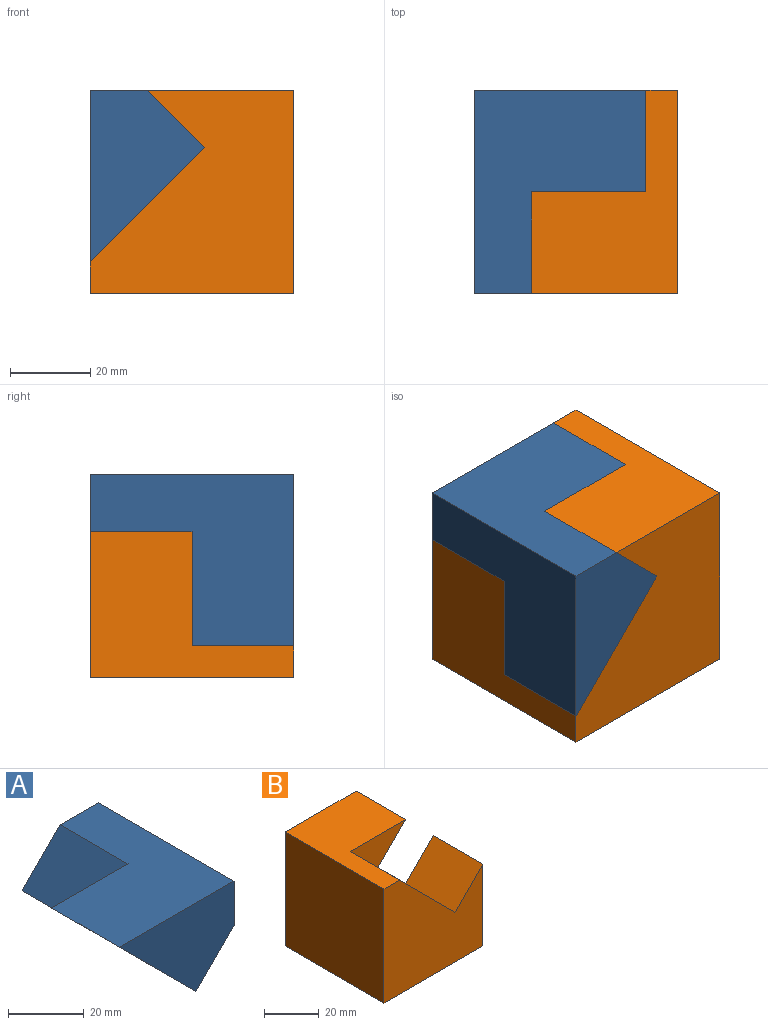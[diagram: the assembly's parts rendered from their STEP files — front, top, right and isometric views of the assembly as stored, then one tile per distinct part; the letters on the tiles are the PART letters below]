
ASSEMBLY  parts=2 mates=1
PART A: 9 faces, bbox 42.9x50.8x42.9 mm
  f0: plane 25.4x14.29mm, normal (-0.71,0,0.71), area 513.2mm2, adj f1,f3,f4,f8
  f1: plane 50.8x42.86mm, normal (-0.71,0,-0.71), area 2052.9mm2, adj f0,f2,f3,f4,f5,f6,f7,f8
  f2: plane 50.8x42.86mm, normal (1,0,0), area 1451.6mm2, adj f1,f3,f4,f5,f6,f7
  f3: plane 50.8x42.86mm, normal (0,0,1), area 1451.6mm2, adj f0,f1,f2,f4,f7,f8
  f4: plane 42.86x28.58mm, normal (0,1,0), area 714.5mm2, adj f0,f1,f2,f3
  f5: plane 28.58x14.29mm, normal (0,-1,0), area 204.1mm2, adj f1,f2,f6
  f6: plane 25.4x14.29mm, normal (0.71,0,-0.71), area 513.2mm2, adj f1,f2,f5,f7
  f7: plane 42.86x28.58mm, normal (0,-1,0), area 714.5mm2, adj f1,f2,f3,f6
  f8: plane 28.58x14.29mm, normal (0,1,0), area 204.1mm2, adj f0,f1,f3
PART B: 11 faces, bbox 50.8x50.8x50.8 mm
  f0: plane 28.58x14.29mm, normal (0,-1,0), area 204.1mm2, adj f1,f2,f3
  f1: plane 50.8x42.86mm, normal (0.71,0,0.71), area 2052.9mm2, adj f0,f2,f3,f6,f7,f8,f9,f10
  f2: plane 25.4x14.29mm, normal (0.71,0,-0.71), area 513.2mm2, adj f0,f1,f3,f7
  f3: plane 50.8x36.51mm, normal (0,0,1), area 1129mm2, adj f0,f1,f2,f4,f7,f9
  f4: plane 50.8x50.8mm, normal (-1,0,0), area 2580.6mm2, adj f3,f5,f7,f9
  f5: plane 50.8x50.8mm, normal (0,0,-1), area 2580.6mm2, adj f4,f6,f7,f9
  f6: plane 50.8x36.51mm, normal (1,0,0), area 1129mm2, adj f1,f5,f7,f8,f9,f10
  f7: plane 50.8x50.8mm, normal (0,1,0), area 1866.2mm2, adj f1,f2,f3,f4,f5,f6
  f8: plane 25.4x14.29mm, normal (-0.71,0,0.71), area 513.2mm2, adj f1,f6,f9,f10
  f9: plane 50.8x50.8mm, normal (0,-1,0), area 1866.2mm2, adj f1,f3,f4,f5,f6,f8
  f10: plane 28.58x14.29mm, normal (0,1,0), area 204.1mm2, adj f1,f6,f8
PLACE A rot(axis=(0,-1,0),90deg) t=(0,0,0)mm
PLACE B rot(axis=(0,-1,0),90deg) t=(0,0,0)mm
MATE slider B.f1 <-> A.f1  axis (-0.71,0,0.71) through (-3.97,0,3.97)mm
